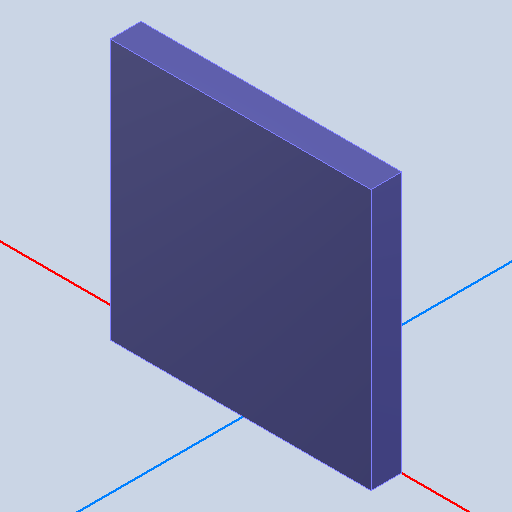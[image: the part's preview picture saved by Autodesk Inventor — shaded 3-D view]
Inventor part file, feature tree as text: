
AUTODESK INVENTOR PART (.ipt)
format: ipt  version: 2022 (Build 260153000, 153)  size: 93,696 bytes
history: native  units: mm
features: other x2, extrude x1
ambient origin geometry x8: Origin, YZ Plane, XZ Plane, XY Plane, X Axis, Y Axis, Z Axis, Center Point
bodies: Body1 (feature_tree)
feature tree (3):
  other  "Твердое тело1"
  extrude  "Выдавливание1"  Depth=1.0mm TaperAngle=0.0deg
  other  "153CLV-0810, 153CLV-0810_1"
